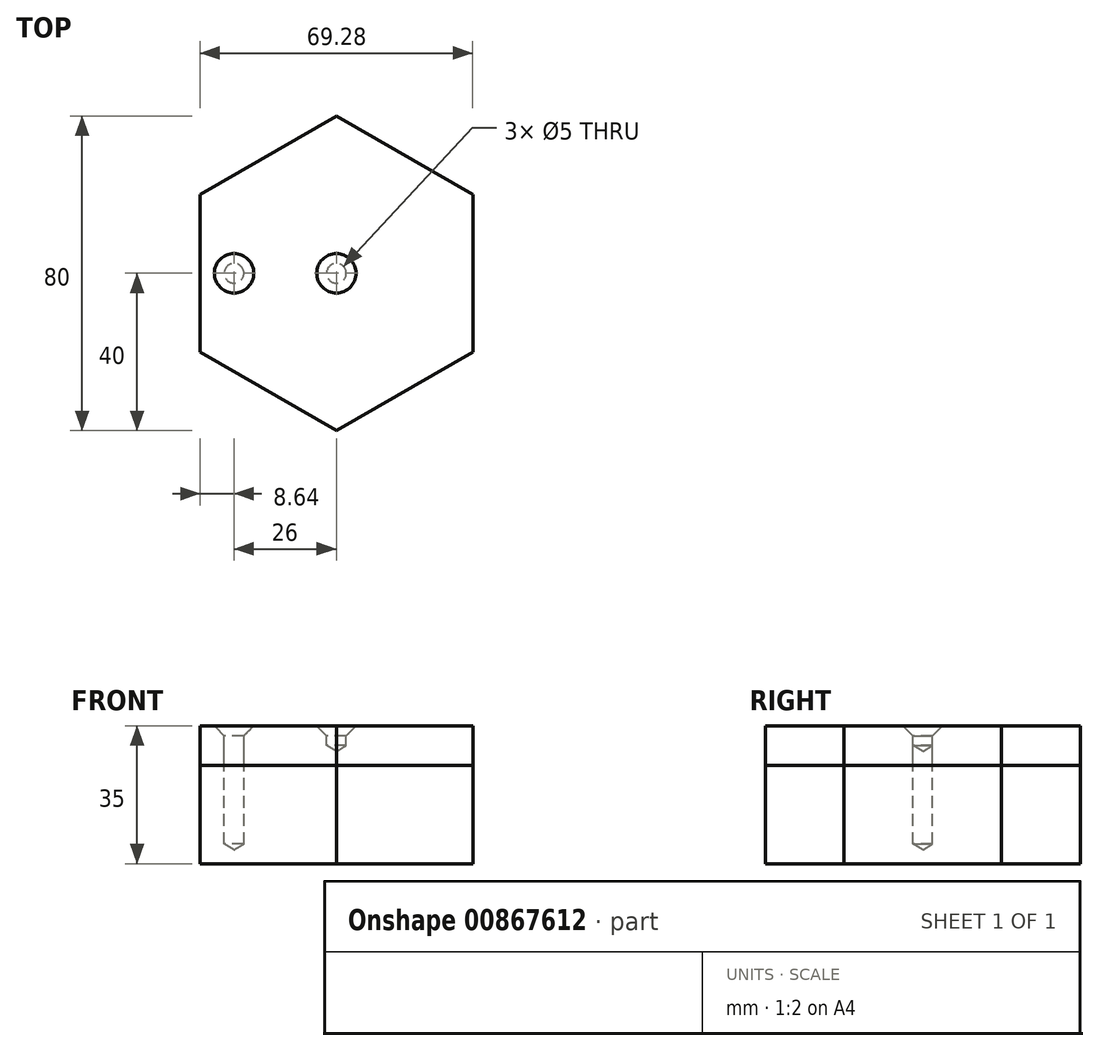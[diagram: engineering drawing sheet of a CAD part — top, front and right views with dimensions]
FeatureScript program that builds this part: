
annotation { "Feature Type Name" : "Feature", "Feature Type Description" : "" }
export const myFeature = defineFeature(function(context is Context, id is Id, definition is map)
    precondition{}
    {
        {
            var Q0;
            Q0=qCreatedBy(makeId("Top.planeOp"),FACE);
            var sketch = newSketch(context, id + "F0", { "sketchPlane" : qUnion([Q0])});
            skCircle(sketch, "E0.cCircle", {"center": v(0, 0) * mm, "radius": 34.64 * mm, "construction": true});
            skLineSegment(sketch, "E0.0", {"start": v(-34.64, 20) * mm, "end": v(0, 40) * mm});
            skLineSegment(sketch, "E0.1", {"start": v(0, 40) * mm, "end": v(34.64, 20) * mm});
            skLineSegment(sketch, "E0.2", {"start": v(34.64, 20) * mm, "end": v(34.64, -20) * mm});
            skLineSegment(sketch, "E0.3", {"start": v(34.64, -20) * mm, "end": v(0, -40) * mm});
            skLineSegment(sketch, "E0.4", {"start": v(0, -40) * mm, "end": v(-34.64, -20) * mm});
            skLineSegment(sketch, "E0.5", {"start": v(-34.64, -20) * mm, "end": v(-34.64, 20) * mm});
            skPoint(sketch, "E0.0.midPoint", {"position": v(-17.32, 30) * mm});
            skSolve(sketch);
        }
        {
            var Q0;
            Q0 = qSketchRegion(id + "F0", true);
            extrude(context, id + "F1", {"entities" : qUnion([Q0]), "depth" : 25 * mm, "offsetDistance" : 25 * mm});
        }
        {
            var Q0;
            Q0=makeQuery(id+"F1.opExtrude","CAP_FACE",FACE,{"disambiguationData":[OSD([sQuery(id+"F0.wireOp",EDGE,"E0.0"),sQuery(id+"F0.wireOp",EDGE,"E0.1"),sQuery(id+"F0.wireOp",EDGE,"E0.2"),sQuery(id+"F0.wireOp",EDGE,"E0.3"),sQuery(id+"F0.wireOp",EDGE,"E0.4"),sQuery(id+"F0.wireOp",EDGE,"E0.5")])],"isStart":false});
            var sketch = newSketch(context, id + "F2", { "sketchPlane" : qUnion([Q0])});
            skLineSegment(sketch, "E1.0", {"start": v(0, 40) * mm, "end": v(-34.64, 20) * mm});
            skLineSegment(sketch, "E1.1", {"start": v(-34.64, -20) * mm, "end": v(0, -40) * mm});
            skLineSegment(sketch, "E1.2", {"start": v(0, -40) * mm, "end": v(34.64, -20) * mm});
            skLineSegment(sketch, "E1.3", {"start": v(-34.64, 20) * mm, "end": v(-34.64, -20) * mm});
            skLineSegment(sketch, "E1.4", {"start": v(34.64, -20) * mm, "end": v(34.64, 20) * mm});
            skLineSegment(sketch, "E1.5", {"start": v(34.64, 20) * mm, "end": v(0, 40) * mm});
            skSolve(sketch);
        }
        {
            var Q0;
            Q0 = qSketchRegion(id + "F2", true);
            extrude(context, id + "F3", {"entities" : qUnion([Q0]), "depth" : 10 * mm, "offsetDistance" : 25 * mm});
        }
        {
            var Q0;
            Q0=makeQuery(id+"F3.opExtrude","CAP_FACE",FACE,{"disambiguationData":[OSD([sQuery(id+"F2.wireOp",EDGE,"E1.0"),sQuery(id+"F2.wireOp",EDGE,"E1.1"),sQuery(id+"F2.wireOp",EDGE,"E1.2"),sQuery(id+"F2.wireOp",EDGE,"E1.3"),sQuery(id+"F2.wireOp",EDGE,"E1.4"),sQuery(id+"F2.wireOp",EDGE,"E1.5")])],"isStart":false});
            var sketch = newSketch(context, id + "F4", { "sketchPlane" : qUnion([Q0])});
            skPoint(sketch, "E2", {"position": v(-26, 0) * mm});
            skSolve(sketch);
        }
        {
            var Q0;
            Q0=sQuery(id+"F4.wireOp",VERTEX,"E2");
            var Q1;
            Q1=makeQuery(id+"F1.opExtrude","SWEPT_BODY",BODY,{"disambiguationData":[OSD([sQuery(id+"F0.wireOp",EDGE,"E0.0"),sQuery(id+"F0.wireOp",EDGE,"E0.1"),sQuery(id+"F0.wireOp",EDGE,"E0.2"),sQuery(id+"F0.wireOp",EDGE,"E0.3"),sQuery(id+"F0.wireOp",EDGE,"E0.4"),sQuery(id+"F0.wireOp",EDGE,"E0.5")])]});
            var Q2;
            Q2=makeQuery(id+"F3.opExtrude","SWEPT_BODY",BODY,{"disambiguationData":[OSD([sQuery(id+"F2.wireOp",EDGE,"E1.0"),sQuery(id+"F2.wireOp",EDGE,"E1.1"),sQuery(id+"F2.wireOp",EDGE,"E1.2"),sQuery(id+"F2.wireOp",EDGE,"E1.3"),sQuery(id+"F2.wireOp",EDGE,"E1.4"),sQuery(id+"F2.wireOp",EDGE,"E1.5")])]});
            hole(context, id + "F5", {"style" : HoleStyle.C_SINK, "endStyle" : HoleEndStyle.BLIND, "holeDiameter" : 5 * mm, "cSinkDiameter" : 10 * mm, "cSinkAngle" : 90 * degree, "majorDiameter" : 5 * mm, "holeDepth" : 30 * mm, "isTappedThrough" : true, "tappedDepth" : 12 * mm, "tapClearance" : 3, "startFromSketch" : true, "locations" : qUnion([Q0]), "scope" : qUnion([Q1, Q2])});
        }
        {
            var Q0;
            Q0=makeQuery(id+"F3.opExtrude","CAP_FACE",FACE,{"disambiguationData":[OSD([sQuery(id+"F2.wireOp",EDGE,"E1.0"),sQuery(id+"F2.wireOp",EDGE,"E1.1"),sQuery(id+"F2.wireOp",EDGE,"E1.2"),sQuery(id+"F2.wireOp",EDGE,"E1.3"),sQuery(id+"F2.wireOp",EDGE,"E1.4"),sQuery(id+"F2.wireOp",EDGE,"E1.5")])],"isStart":false});
            var sketch = newSketch(context, id + "F6", { "sketchPlane" : qUnion([Q0])});
            skCircle(sketch, "E3.0", {"center": v(-26, 0) * mm, "radius": 5 * mm});
            skSolve(sketch);
        }
        {
            var Q0;
            Q0 = qSketchRegion(id + "F6", true);
            var Q1;
            Q1=makeQuery(id+"F1.opExtrude","CAP_FACE",FACE,{"disambiguationData":[OSD([sQuery(id+"F0.wireOp",EDGE,"E0.0"),sQuery(id+"F0.wireOp",EDGE,"E0.1"),sQuery(id+"F0.wireOp",EDGE,"E0.2"),sQuery(id+"F0.wireOp",EDGE,"E0.3"),sQuery(id+"F0.wireOp",EDGE,"E0.4"),sQuery(id+"F0.wireOp",EDGE,"E0.5")])],"isStart":true});
            extrude(context, id + "F7", {"entities" : qUnion([Q0]), "endBound" : BoundingType.UP_TO_SURFACE, "oppositeDirection" : true, "depth" : 25 * mm, "endBoundEntityFace" : qUnion([Q1]), "offsetDistance" : 25 * mm});
        }
        {
            var Q0;
            Q0=makeQuery(id+"F3.opExtrude","SWEPT_BODY",BODY,{"disambiguationData":[OSD([sQuery(id+"F2.wireOp",EDGE,"E1.0"),sQuery(id+"F2.wireOp",EDGE,"E1.1"),sQuery(id+"F2.wireOp",EDGE,"E1.2"),sQuery(id+"F2.wireOp",EDGE,"E1.3"),sQuery(id+"F2.wireOp",EDGE,"E1.4"),sQuery(id+"F2.wireOp",EDGE,"E1.5")])]});
            var Q1;
            Q1=makeQuery(id+"F1.opExtrude","SWEPT_BODY",BODY,{"disambiguationData":[OSD([sQuery(id+"F0.wireOp",EDGE,"E0.0"),sQuery(id+"F0.wireOp",EDGE,"E0.1"),sQuery(id+"F0.wireOp",EDGE,"E0.2"),sQuery(id+"F0.wireOp",EDGE,"E0.3"),sQuery(id+"F0.wireOp",EDGE,"E0.4"),sQuery(id+"F0.wireOp",EDGE,"E0.5")])]});
            var Q2;
            Q2=makeQuery(id+"F7.opExtrude","SWEPT_BODY",BODY,{"disambiguationData":[OSD([sQuery(id+"F6.wireOp",EDGE,"E3.0")])]});
            booleanBodies(context, id + "F8", {"operationType" : BooleanOperationType.SUBTRACTION, "tools" : qUnion([Q0, Q1]), "targets" : qUnion([Q2]), "keepTools" : true});
        }
        {
            var Q0;
            Q0=makeQuery(id+"F3.opExtrude","CAP_FACE",FACE,{"disambiguationData":[OSD([sQuery(id+"F2.wireOp",EDGE,"E1.0"),sQuery(id+"F2.wireOp",EDGE,"E1.1"),sQuery(id+"F2.wireOp",EDGE,"E1.2"),sQuery(id+"F2.wireOp",EDGE,"E1.3"),sQuery(id+"F2.wireOp",EDGE,"E1.4"),sQuery(id+"F2.wireOp",EDGE,"E1.5")])],"isStart":false});
            var sketch = newSketch(context, id + "F9", { "sketchPlane" : qUnion([Q0])});
            skPoint(sketch, "E4", {"position": v(0, 0) * mm});
            skSolve(sketch);
        }
        {
            var Q0;
            Q0=sQuery(id+"F9.wireOp",VERTEX,"E4");
            var Q1;
            Q1=makeQuery(id+"F3.opExtrude","SWEPT_BODY",BODY,{"disambiguationData":[OSD([sQuery(id+"F2.wireOp",EDGE,"E1.0"),sQuery(id+"F2.wireOp",EDGE,"E1.1"),sQuery(id+"F2.wireOp",EDGE,"E1.2"),sQuery(id+"F2.wireOp",EDGE,"E1.3"),sQuery(id+"F2.wireOp",EDGE,"E1.4"),sQuery(id+"F2.wireOp",EDGE,"E1.5")])]});
            hole(context, id + "F10", {"style" : HoleStyle.C_SINK, "endStyle" : HoleEndStyle.BLIND, "holeDiameter" : 5 * mm, "cSinkDiameter" : 10 * mm, "cSinkAngle" : 90 * degree, "majorDiameter" : 5 * mm, "holeDepth" : 5 * mm, "isTappedThrough" : true, "tappedDepth" : 12 * mm, "tapClearance" : 3, "startFromSketch" : true, "locations" : qUnion([Q0]), "scope" : qUnion([Q1])});
        }
        {
            var Q0;
            Q0=makeQuery(id+"F3.opExtrude","CAP_FACE",FACE,{"disambiguationData":[OSD([sQuery(id+"F2.wireOp",EDGE,"E1.0"),sQuery(id+"F2.wireOp",EDGE,"E1.1"),sQuery(id+"F2.wireOp",EDGE,"E1.2"),sQuery(id+"F2.wireOp",EDGE,"E1.3"),sQuery(id+"F2.wireOp",EDGE,"E1.4"),sQuery(id+"F2.wireOp",EDGE,"E1.5")])],"isStart":false});
            var sketch = newSketch(context, id + "F11", { "sketchPlane" : qUnion([Q0])});
            skCircle(sketch, "E5.0", {"center": v(0, 0) * mm, "radius": 5 * mm});
            skSolve(sketch);
        }
        {
            var Q0;
            Q0 = qSketchRegion(id + "F11", true);
            var Q1;
            Q1=makeQuery(id+"F3.opExtrude","CAP_FACE",FACE,{"disambiguationData":[OSD([sQuery(id+"F2.wireOp",EDGE,"E1.0"),sQuery(id+"F2.wireOp",EDGE,"E1.1"),sQuery(id+"F2.wireOp",EDGE,"E1.2"),sQuery(id+"F2.wireOp",EDGE,"E1.3"),sQuery(id+"F2.wireOp",EDGE,"E1.4"),sQuery(id+"F2.wireOp",EDGE,"E1.5")])],"isStart":true});
            extrude(context, id + "F12", {"entities" : qUnion([Q0]), "endBound" : BoundingType.UP_TO_SURFACE, "oppositeDirection" : true, "depth" : 25 * mm, "endBoundEntityFace" : qUnion([Q1]), "offsetDistance" : 25 * mm});
        }
        {
            var Q0;
            Q0=makeQuery(id+"F3.opExtrude","SWEPT_BODY",BODY,{"disambiguationData":[OSD([sQuery(id+"F2.wireOp",EDGE,"E1.0"),sQuery(id+"F2.wireOp",EDGE,"E1.1"),sQuery(id+"F2.wireOp",EDGE,"E1.2"),sQuery(id+"F2.wireOp",EDGE,"E1.3"),sQuery(id+"F2.wireOp",EDGE,"E1.4"),sQuery(id+"F2.wireOp",EDGE,"E1.5")])]});
            var Q1;
            Q1=makeQuery(id+"F12.opExtrude","SWEPT_BODY",BODY,{"disambiguationData":[OSD([sQuery(id+"F11.wireOp",EDGE,"E5.0")])]});
            booleanBodies(context, id + "F13", {"operationType" : BooleanOperationType.SUBTRACTION, "tools" : qUnion([Q0]), "targets" : qUnion([Q1]), "keepTools" : true});
        }
    });
